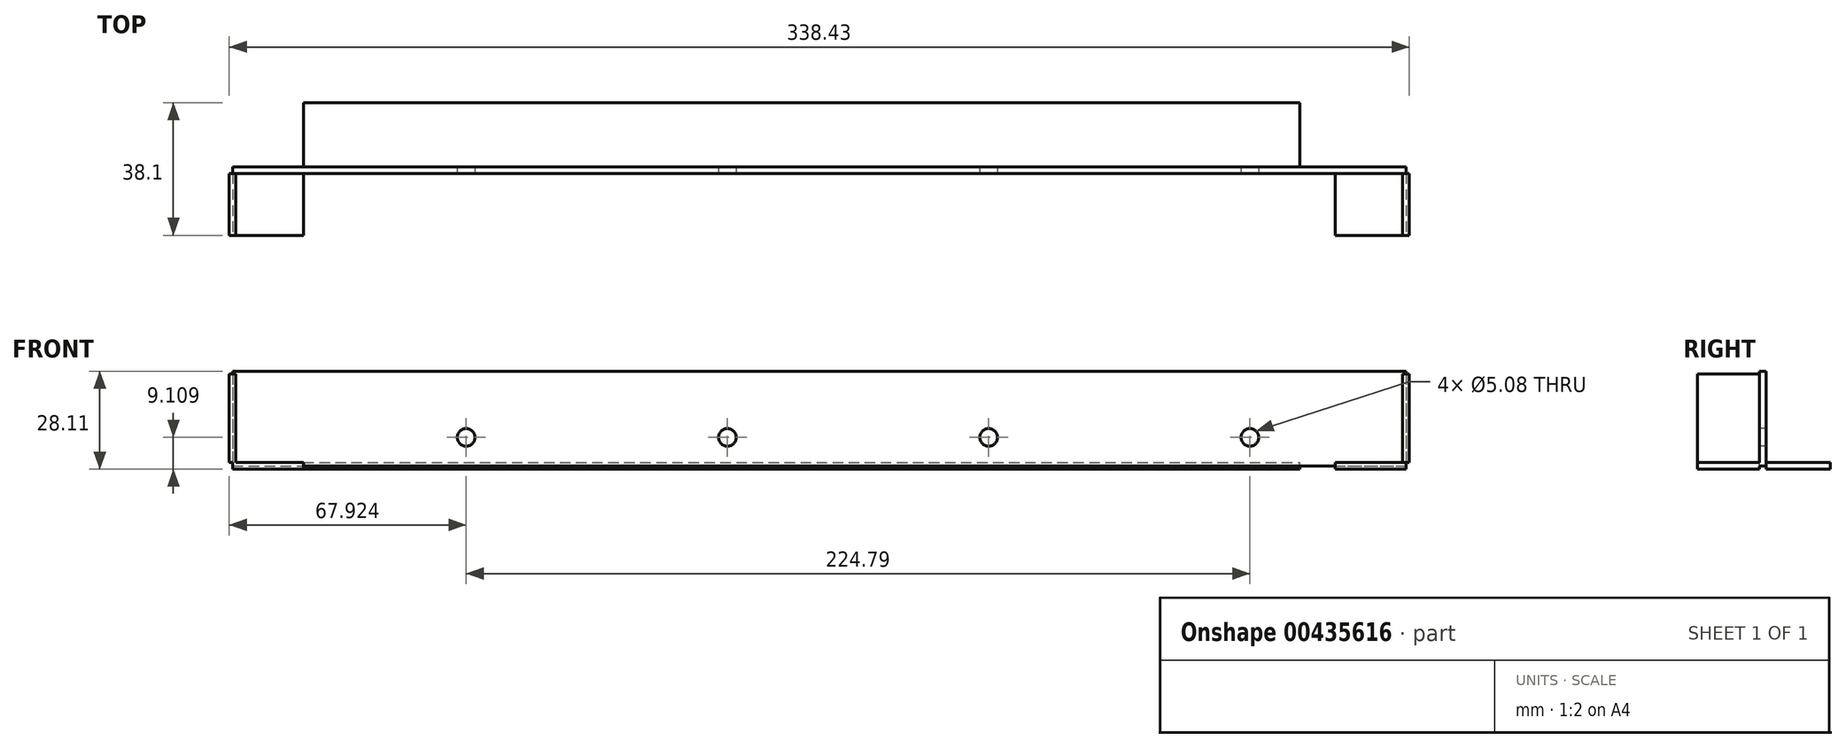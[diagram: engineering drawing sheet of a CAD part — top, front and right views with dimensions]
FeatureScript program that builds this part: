
annotation { "Feature Type Name" : "Feature", "Feature Type Description" : "" }
export const myFeature = defineFeature(function(context is Context, id is Id, definition is map)
    precondition{}
    {
        {
            var Q0;
            Q0=qCreatedBy(makeId("Front.planeOp"),FACE);
            var sketch = newSketch(context, id + "F0", { "sketchPlane" : qUnion([Q0])});
            skLineSegment(sketch, "E0.bottom", {"start": v(-151.02, 13.87) * mm, "end": v(185.53, 13.87) * mm});
            skLineSegment(sketch, "E0.top", {"start": v(-151.02, -13.3) * mm, "end": v(185.53, -13.3) * mm});
            skLineSegment(sketch, "E0.left", {"start": v(-151.02, 13.87) * mm, "end": v(-151.02, -13.3) * mm});
            skLineSegment(sketch, "E0.right", {"start": v(185.53, 13.87) * mm, "end": v(185.53, -13.3) * mm});
            skSolve(sketch);
        }
        {
            var Q0;
            Q0=makeQuery(id+"F0.imprint","IMPRINT",FACE,{"disambiguationData":[TD([[makeQuery(id+"F0.imprint","IMPRINT",EDGE,{"derivedFrom":sQuery(id+"F0.wireOp",EDGE,"E0.bottom")}),-1.0]])]});
            extrude(context, id + "F1", {"entities" : qUnion([Q0]), "depth" : 1.88 * mm});
        }
        {
            var Q0;
            Q0=makeQuery(id+"F1.opExtrude","SWEPT_FACE",FACE,{"disambiguationData":[OSD([sQuery(id+"F0.wireOp",EDGE,"E0.top")])]});
            var sketch = newSketch(context, id + "F2", { "sketchPlane" : qUnion([Q0])});
            skLineSegment(sketch, "E1.bottom", {"start": v(-151.02, 1.88) * mm, "end": v(-130.7, 1.88) * mm});
            skLineSegment(sketch, "E1.top", {"start": v(-151.02, 19.66) * mm, "end": v(-130.7, 19.66) * mm});
            skLineSegment(sketch, "E1.left", {"start": v(-151.02, 1.88) * mm, "end": v(-151.02, 19.66) * mm});
            skLineSegment(sketch, "E1.right", {"start": v(-130.7, 1.88) * mm, "end": v(-130.7, 19.66) * mm});
            skLineSegment(sketch, "E2.bottom", {"start": v(185.53, 1.88) * mm, "end": v(165.21, 1.88) * mm});
            skLineSegment(sketch, "E2.top", {"start": v(185.53, 19.66) * mm, "end": v(165.21, 19.66) * mm});
            skLineSegment(sketch, "E2.left", {"start": v(185.53, 1.88) * mm, "end": v(185.53, 19.66) * mm});
            skLineSegment(sketch, "E2.right", {"start": v(165.21, 1.88) * mm, "end": v(165.21, 19.66) * mm});
            skSolve(sketch);
        }
        {
            var Q0;
            Q0=makeQuery(id+"F2.imprint","IMPRINT",FACE,{"disambiguationData":[TD([[makeQuery(id+"F2.imprint","IMPRINT",EDGE,{"derivedFrom":sQuery(id+"F2.wireOp",EDGE,"E1.bottom")}),1.0]])]});
            var Q1;
            Q1=makeQuery(id+"F2.imprint","IMPRINT",FACE,{"disambiguationData":[TD([[makeQuery(id+"F2.imprint","IMPRINT",EDGE,{"derivedFrom":sQuery(id+"F2.wireOp",EDGE,"E2.bottom")}),1.0]])]});
            extrude(context, id + "F3", {"entities" : qUnion([Q0, Q1]), "operationType" : NewBodyOperationType.ADD, "depth" : 1.88 * mm, "symmetric" : true});
        }
        {
            var Q0;
            Q0=makeQuery(id+"F3.boolean.opBoolean","MERGE",FACE,{"derivedFrom":[makeQuery(id+"F1.opExtrude","SWEPT_FACE",FACE,{"disambiguationData":[OSD([sQuery(id+"F0.wireOp",EDGE,"E0.left")])]}),makeQuery(id+"F3.opExtrude","SWEPT_FACE",FACE,{"disambiguationData":[OSD([sQuery(id+"F2.wireOp",EDGE,"E1.left")])]})]});
            var sketch = newSketch(context, id + "F4", { "sketchPlane" : qUnion([Q0])});
            skLineSegment(sketch, "E3.bottom", {"start": v(1.88, -12.36) * mm, "end": v(19.66, -12.36) * mm});
            skLineSegment(sketch, "E3.top", {"start": v(1.88, 13.04) * mm, "end": v(19.66, 13.04) * mm});
            skLineSegment(sketch, "E3.left", {"start": v(1.88, -12.36) * mm, "end": v(1.88, 13.04) * mm});
            skLineSegment(sketch, "E3.right", {"start": v(19.66, -12.36) * mm, "end": v(19.66, 13.04) * mm});
            skSolve(sketch);
        }
        {
            var Q0;
            Q0=makeQuery(id+"F4.imprint","IMPRINT",FACE,{"disambiguationData":[TD([[makeQuery(id+"F4.imprint","IMPRINT",EDGE,{"derivedFrom":sQuery(id+"F4.wireOp",EDGE,"E3.bottom")}),1.0]])]});
            extrude(context, id + "F5", {"entities" : qUnion([Q0]), "operationType" : NewBodyOperationType.ADD, "depth" : 1.88 * mm, "symmetric" : true});
        }
        {
            var Q0;
            Q0=makeQuery(id+"F3.boolean.opBoolean","MERGE",FACE,{"derivedFrom":[makeQuery(id+"F1.opExtrude","SWEPT_FACE",FACE,{"disambiguationData":[OSD([sQuery(id+"F0.wireOp",EDGE,"E0.right")])]}),makeQuery(id+"F3.opExtrude","SWEPT_FACE",FACE,{"disambiguationData":[OSD([sQuery(id+"F2.wireOp",EDGE,"E2.left")])]})]});
            var sketch = newSketch(context, id + "F6", { "sketchPlane" : qUnion([Q0])});
            skLineSegment(sketch, "E4.bottom", {"start": v(-1.88, -13.3) * mm, "end": v(-19.66, -13.3) * mm});
            skLineSegment(sketch, "E4.top", {"start": v(-1.88, 13.04) * mm, "end": v(-19.66, 13.04) * mm});
            skLineSegment(sketch, "E4.left", {"start": v(-1.88, -13.3) * mm, "end": v(-1.88, 13.04) * mm});
            skLineSegment(sketch, "E4.right", {"start": v(-19.66, -13.3) * mm, "end": v(-19.66, 13.04) * mm});
            skSolve(sketch);
        }
        {
            var Q0;
            {var subQ0=sQuery(id+"F6.wireOp",EDGE,"E4.top");Q0=makeQuery(id+"F6.imprint","IMPRINT",FACE,{"disambiguationData":[TD([[makeQuery(id+"F6.imprint","IMPRINT",EDGE,{"derivedFrom":subQ0}),1.0]])]});}
            extrude(context, id + "F7", {"entities" : qUnion([Q0]), "depth" : 1.88 * mm, "symmetric" : true});
        }
        {
            var Q0;
            Q0=makeQuery(id+"F1.opExtrude","SWEPT_FACE",FACE,{"disambiguationData":[OSD([sQuery(id+"F0.wireOp",EDGE,"E0.top")])]});
            var sketch = newSketch(context, id + "F8", { "sketchPlane" : qUnion([Q0])});
            skLineSegment(sketch, "E5.bottom", {"start": v(-130.7, 1.88) * mm, "end": v(155.05, 1.88) * mm});
            skLineSegment(sketch, "E5.top", {"start": v(-130.7, -18.44) * mm, "end": v(155.05, -18.44) * mm});
            skLineSegment(sketch, "E5.left", {"start": v(-130.7, 1.88) * mm, "end": v(-130.7, -18.44) * mm});
            skLineSegment(sketch, "E5.right", {"start": v(155.05, 1.88) * mm, "end": v(155.05, -18.44) * mm});
            skSolve(sketch);
        }
        {
            var Q0;
            {var subQ0=sQuery(id+"F8.wireOp",EDGE,"E5.top");Q0=makeQuery(id+"F8.imprint","IMPRINT",FACE,{"disambiguationData":[TD([[makeQuery(id+"F8.imprint","IMPRINT",EDGE,{"derivedFrom":subQ0}),1.0]])]});}
            extrude(context, id + "F9", {"entities" : qUnion([Q0]), "operationType" : NewBodyOperationType.ADD, "depth" : 1.88 * mm, "symmetric" : true});
        }
        {
            var Q0;
            Q0=makeQuery(id+"F1.opExtrude","CAP_FACE",FACE,{"disambiguationData":[OSD([sQuery(id+"F0.wireOp",EDGE,"E0.bottom"),sQuery(id+"F0.wireOp",EDGE,"E0.top"),sQuery(id+"F0.wireOp",EDGE,"E0.left"),sQuery(id+"F0.wireOp",EDGE,"E0.right")])],"isStart":false});
            var sketch = newSketch(context, id + "F10", { "sketchPlane" : qUnion([Q0])});
            skPoint(sketch, "E6", {"position": v(-84.04, -5.13) * mm});
            skPoint(sketch, "E7", {"position": v(-9.1, -5.13) * mm});
            skPoint(sketch, "E8", {"position": v(65.82, -5.13) * mm});
            skPoint(sketch, "E9", {"position": v(140.75, -5.13) * mm});
            skSolve(sketch);
        }
        {
            var Q0;
            Q0=sQuery(id+"F10.wireOp",VERTEX,"E6");
            var Q1;
            Q1=sQuery(id+"F10.wireOp",VERTEX,"E7");
            var Q2;
            Q2=sQuery(id+"F10.wireOp",VERTEX,"E8");
            var Q3;
            Q3=sQuery(id+"F10.wireOp",VERTEX,"E9");
            var Q4;
            Q4=makeQuery(id+"F1.opExtrude","SWEPT_BODY",BODY,{"disambiguationData":[OSD([sQuery(id+"F0.wireOp",EDGE,"E0.bottom"),sQuery(id+"F0.wireOp",EDGE,"E0.top"),sQuery(id+"F0.wireOp",EDGE,"E0.left"),sQuery(id+"F0.wireOp",EDGE,"E0.right")])]});
            hole(context, id + "F11", {"style" : HoleStyle.SIMPLE, "endStyle" : HoleEndStyle.BLIND, "holeDiameter" : 5.08 * mm, "holeDepth" : 25.4 * mm, "isTappedThrough" : true, "tappedDepth" : 12.7 * mm, "tapClearance" : 3, "locations" : qUnion([Q0, Q1, Q2, Q3]), "scope" : qUnion([Q4])});
        }
    });
